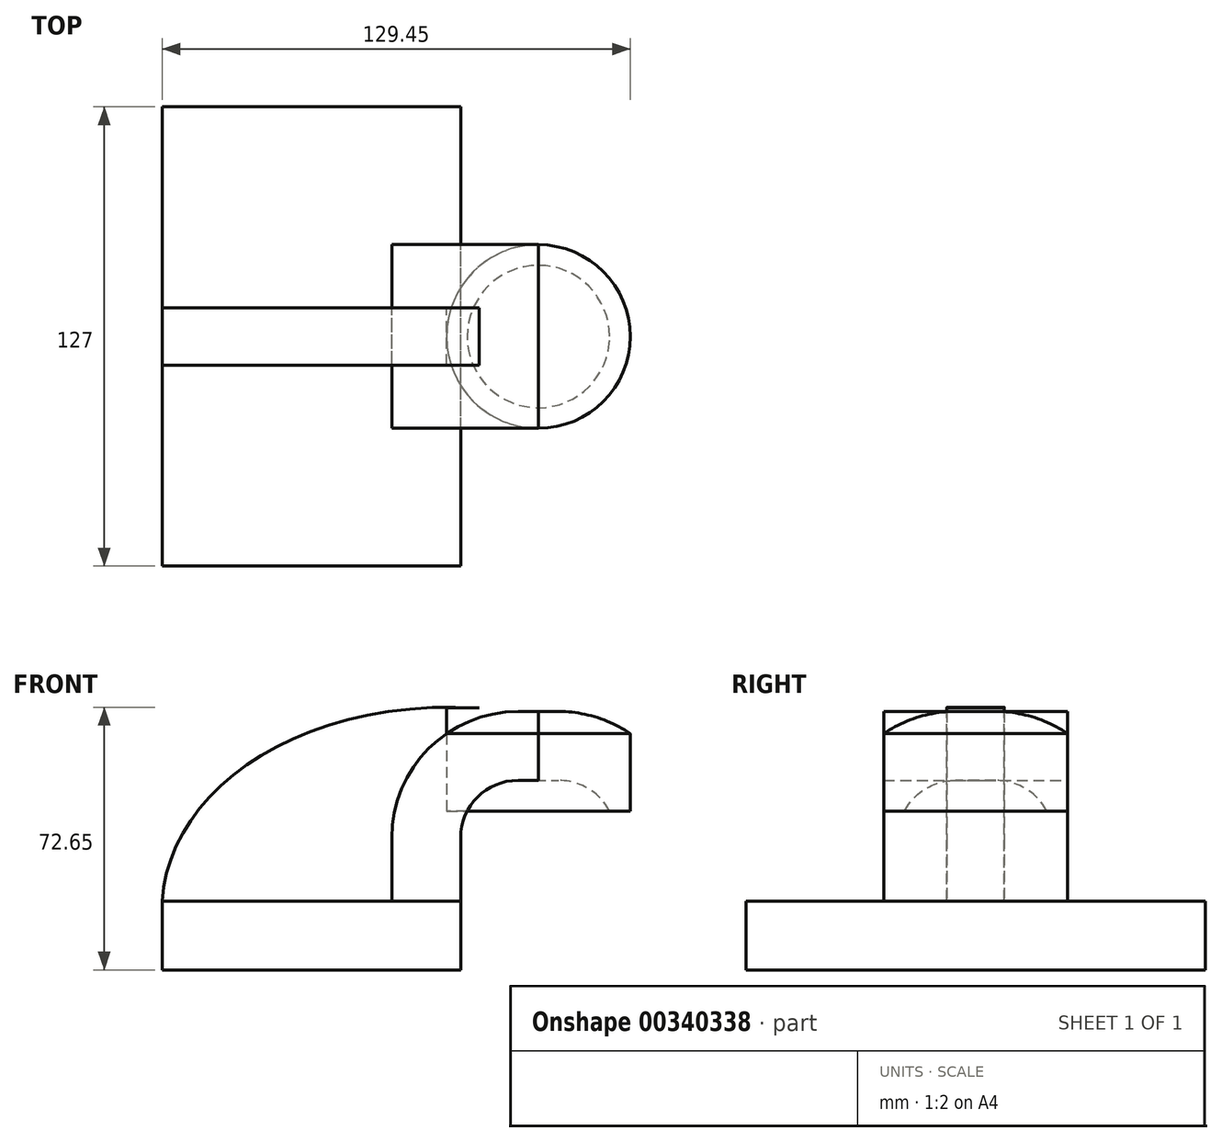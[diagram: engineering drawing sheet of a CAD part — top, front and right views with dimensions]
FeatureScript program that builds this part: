
annotation { "Feature Type Name" : "Feature", "Feature Type Description" : "" }
export const myFeature = defineFeature(function(context is Context, id is Id, definition is map)
    precondition{}
    {
        {
            var Q0;
            Q0=qCreatedBy(makeId("Front.planeOp"),FACE);
            var sketch = newSketch(context, id + "F0", { "sketchPlane" : qUnion([Q0])});
            skLineSegment(sketch, "E0.bottom", {"start": v(37.37, 62.92) * mm, "end": v(88.17, 62.92) * mm});
            skLineSegment(sketch, "E0.top", {"start": v(37.37, 34.34) * mm, "end": v(88.17, 34.34) * mm});
            skLineSegment(sketch, "E0.left", {"start": v(37.37, 62.92) * mm, "end": v(37.37, 34.34) * mm});
            skLineSegment(sketch, "E0.right", {"start": v(88.17, 62.92) * mm, "end": v(88.17, 34.34) * mm});
            skLineSegment(sketch, "E1.bottom", {"start": v(41.28, -9.53) * mm, "end": v(-41.28, -9.53) * mm});
            skLineSegment(sketch, "E1.top", {"start": v(41.28, 9.53) * mm, "end": v(-41.28, 9.53) * mm});
            skLineSegment(sketch, "E1.left", {"start": v(41.28, -9.53) * mm, "end": v(41.28, 9.53) * mm});
            skLineSegment(sketch, "E1.right", {"start": v(-41.28, -9.53) * mm, "end": v(-41.28, 9.53) * mm});
            skPoint(sketch, "E1.middle", {"position": v(0, 0) * mm});
            skLineSegment(sketch, "E2", {"start": v(41.28, 9.53) * mm, "end": v(41.28, 27) * mm});
            skArc(sketch, "E3", {"start": v(41.27, 27) * mm, "mid": v(45.92, 38.23) * mm, "end": v(57.15, 42.88) * mm});
            skLineSegment(sketch, "E4", {"start": v(57.15, 42.88) * mm, "end": v(101.6, 42.88) * mm});
            skLineSegment(sketch, "E5.0", {"start": v(57.15, 61.93) * mm, "end": v(62.77, 61.93) * mm});
            skArc(sketch, "E5.1", {"start": v(22.22, 27) * mm, "mid": v(32.45, 51.7) * mm, "end": v(57.15, 61.93) * mm});
            skLineSegment(sketch, "E5.2", {"start": v(22.22, 18.33) * mm, "end": v(22.22, 27) * mm});
            skFitSpline(sketch, "E6", {"points": [v(-41.28, 9.53) * mm, v(57.15, 61.93) * mm], "startDerivative": vector(6.32, 95.78) * mm, "endDerivative": vector(171.45, -22.11) * mm});
            skLineSegment(sketch, "E7", {"start": v(22.22, 18.33) * mm, "end": v(22.22, 9.53) * mm});
            skPoint(sketch, "E8", {"position": v(112.14, -9.22) * mm});
            skPoint(sketch, "E9", {"position": v(112.14, 62.92) * mm});
            skLineSegment(sketch, "E10", {"start": v(112.14, 62.92) * mm, "end": v(112.14, -9.22) * mm});
            skLineSegment(sketch, "E11", {"start": v(62.77, 61.93) * mm, "end": v(62.77, 34.34) * mm});
            skPoint(sketch, "E12", {"position": v(62.77, 62.92) * mm});
            skPoint(sketch, "E13", {"position": v(62.77, 34.34) * mm});
            skLineSegment(sketch, "E14", {"start": v(62.77, 34.34) * mm, "end": v(62.77, 62.92) * mm});
            skLineSegment(sketch, "E15.bottom", {"start": v(37.37, 62.92) * mm, "end": v(62.77, 62.92) * mm});
            skLineSegment(sketch, "E15.top", {"start": v(37.37, 34.34) * mm, "end": v(62.77, 34.34) * mm});
            skLineSegment(sketch, "E15.right", {"start": v(62.77, 62.92) * mm, "end": v(62.77, 34.34) * mm});
            skPoint(sketch, "E16", {"position": v(80.38, 62.92) * mm});
            skPoint(sketch, "E17", {"position": v(62.77, 42.88) * mm});
            skSolve(sketch);
        }
        {
            var Q0;
            Q0=makeQuery(id+"F0.imprint","IMPRINT",FACE,{"disambiguationData":[TD([[makeQuery(id+"F0.imprint","IMPRINT",EDGE,{"derivedFrom":sQuery(id+"F0.wireOp",EDGE,"E1.bottom")}),-1.0]])]});
            extrude(context, id + "F1", {"entities" : qUnion([Q0]), "depth" : 127 * mm, "symmetric" : true});
        }
        {
            var Q0;
            {var subQ0=sQuery(id+"F0.wireOp",EDGE,"E5.2");Q0=makeQuery(id+"F0.imprint","IMPRINT",FACE,{"disambiguationData":[TD([[makeQuery(id+"F0.imprint","IMPRINT",EDGE,{"derivedFrom":subQ0}),1.0]])]});}
            extrude(context, id + "F2", {"entities" : qUnion([Q0]), "operationType" : NewBodyOperationType.ADD, "depth" : 15.88 * mm, "symmetric" : true});
        }
        {
            var Q0;
            {var subQ0=sQuery(id+"F0.wireOp",EDGE,"E5.0");Q0=makeQuery(id+"F0.imprint","IMPRINT",FACE,{"disambiguationData":[TD([[makeQuery(id+"F0.imprint","IMPRINT",EDGE,{"derivedFrom":subQ0}),-1.0]])]});}
            var Q1;
            Q1=sQuery(id+"F0.wireOp",EDGE,"E14");
            revolve(context, id + "F3", {"entities" : qUnion([Q0]), "axis" : qUnion([Q1]), "revolveType" : RevolveType.FULL});
        }
        {
            var Q0;
            {var subQ0=sQuery(id+"F0.wireOp",EDGE,"E5.0");Q0=makeQuery(id+"F0.imprint","IMPRINT",FACE,{"disambiguationData":[TD([[makeQuery(id+"F0.imprint","IMPRINT",EDGE,{"derivedFrom":subQ0}),-1.0]])]});}
            var Q1;
            {var subQ0=sQuery(id+"F0.wireOp",EDGE,"E2");Q1=makeQuery(id+"F0.imprint","IMPRINT",FACE,{"disambiguationData":[TD([[makeQuery(id+"F0.imprint","IMPRINT",EDGE,{"derivedFrom":subQ0}),1.0]])]});}
            extrude(context, id + "F4", {"entities" : qUnion([Q0, Q1]), "depth" : 50.8 * mm, "symmetric" : true});
        }
    });
